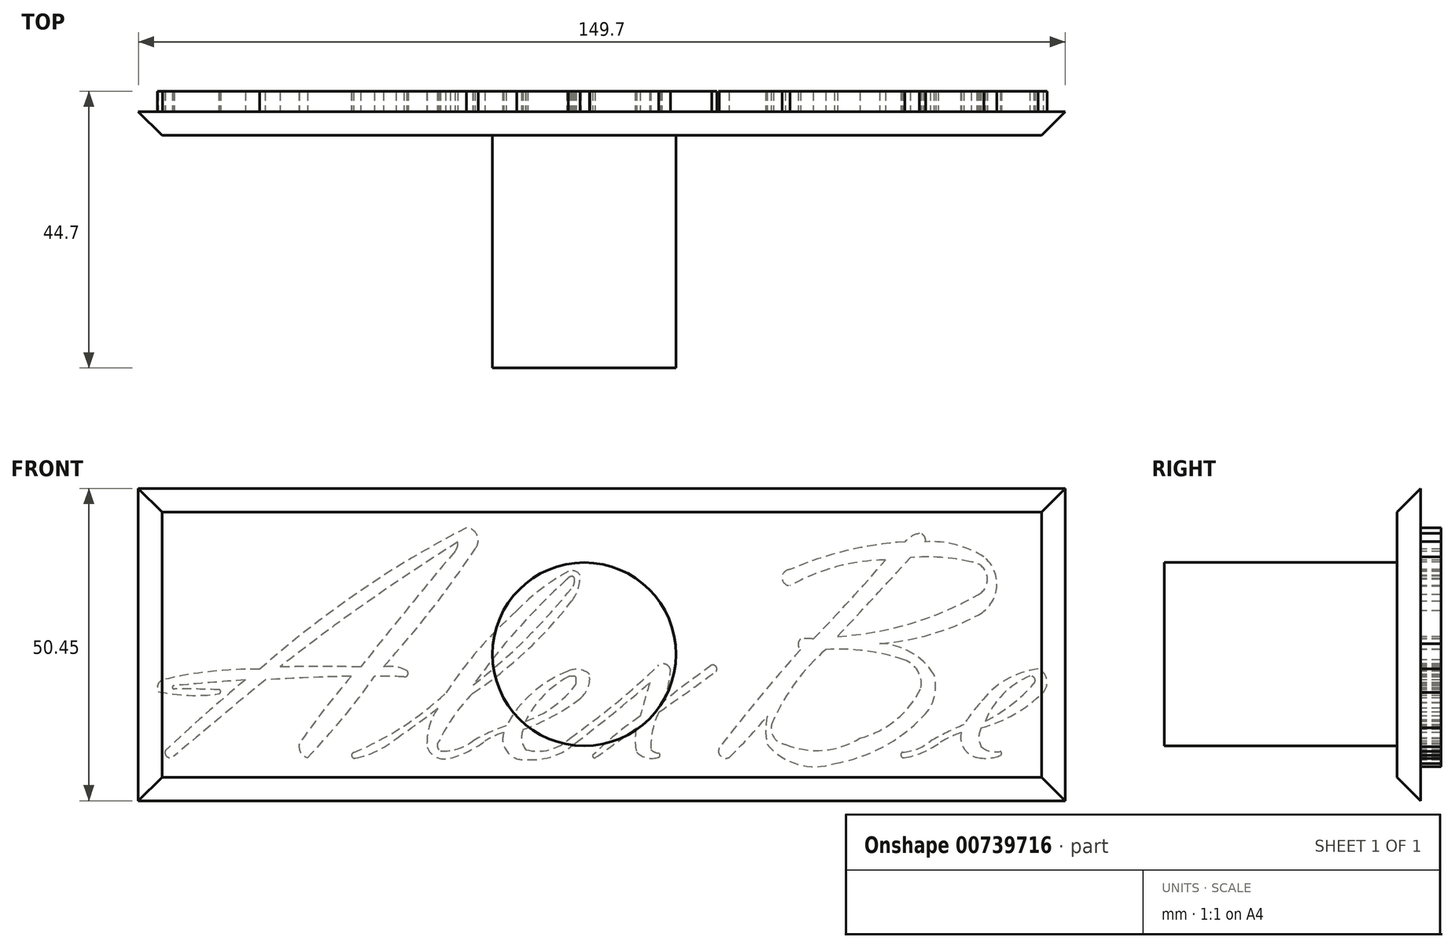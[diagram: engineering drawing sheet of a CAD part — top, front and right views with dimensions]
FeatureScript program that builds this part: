
annotation { "Feature Type Name" : "Feature", "Feature Type Description" : "" }
export const myFeature = defineFeature(function(context is Context, id is Id, definition is map)
    precondition{}
    {
        {
            var Q0;
            Q0=qCreatedBy(makeId("Front.planeOp"),FACE);
            var sketch = newSketch(context, id + "F0", { "sketchPlane" : qUnion([Q0])});
            skArc(sketch, "E0", {"start": v(-67.67, -1.55) * mm, "mid": v(-67.34, -2.53) * mm, "end": v(-66.3, -2.45) * mm});
            skArc(sketch, "E1", {"start": v(-54.74, 9.9) * mm, "mid": v(-61.3, 4.28) * mm, "end": v(-67.67, -1.55) * mm});
            skArc(sketch, "E2", {"start": v(-54.74, 9.9) * mm, "mid": v(-60.47, 9.47) * mm, "end": v(-66.2, 8.99) * mm});
            skArc(sketch, "E3", {"start": v(-66.2, 8.99) * mm, "mid": v(-66.51, 8.7) * mm, "end": v(-66.2, 8.43) * mm});
            skArc(sketch, "E4", {"start": v(-58.86, 8.3) * mm, "mid": v(-62.53, 8.42) * mm, "end": v(-66.2, 8.43) * mm});
            skArc(sketch, "E5", {"start": v(-59, 7.66) * mm, "mid": v(-58.74, 7.94) * mm, "end": v(-58.86, 8.3) * mm});
            skArc(sketch, "E6", {"start": v(-68.8, 8.02) * mm, "mid": v(-63.92, 7.4) * mm, "end": v(-59, 7.66) * mm});
            skArc(sketch, "E7", {"start": v(-68.12, 9.9) * mm, "mid": v(-68.87, 9.1) * mm, "end": v(-68.8, 8.02) * mm});
            skArc(sketch, "E8", {"start": v(-52.44, 11.62) * mm, "mid": v(-60.34, 11.27) * mm, "end": v(-68.12, 9.9) * mm});
            skArc(sketch, "E9", {"start": v(-19.01, 34.51) * mm, "mid": v(-36.44, 24.1) * mm, "end": v(-52.44, 11.62) * mm});
            skArc(sketch, "E10", {"start": v(-17.65, 31.1) * mm, "mid": v(-17.27, 33.22) * mm, "end": v(-19.01, 34.51) * mm});
            skArc(sketch, "E11", {"start": v(-32.44, 12.02) * mm, "mid": v(-24.67, 21.27) * mm, "end": v(-17.65, 31.1) * mm});
            skArc(sketch, "E12", {"start": v(-28.66, 11.42) * mm, "mid": v(-30.5, 12.02) * mm, "end": v(-32.44, 12.02) * mm});
            skArc(sketch, "E13", {"start": v(-29.11, 10.4) * mm, "mid": v(-28.5, 10.74) * mm, "end": v(-28.66, 11.42) * mm});
            skArc(sketch, "E14", {"start": v(-29.11, 10.4) * mm, "mid": v(-31.5, 10.5) * mm, "end": v(-33.87, 10.48) * mm});
            skArc(sketch, "E15", {"start": v(-44.7, -2.66) * mm, "mid": v(-39.03, 3.7) * mm, "end": v(-33.87, 10.48) * mm});
            skArc(sketch, "E16", {"start": v(-46.03, -0.44) * mm, "mid": v(-45.8, -1.81) * mm, "end": v(-44.7, -2.66) * mm});
            skArc(sketch, "E17", {"start": v(-37.62, 10.48) * mm, "mid": v(-41.98, 5.14) * mm, "end": v(-46.03, -0.44) * mm});
            skArc(sketch, "E18", {"start": v(-37.62, 10.48) * mm, "mid": v(-44.57, 10.29) * mm, "end": v(-51.51, 9.92) * mm});
            skArc(sketch, "E19", {"start": v(-51.51, 9.92) * mm, "mid": v(-58.92, 3.75) * mm, "end": v(-66.3, -2.45) * mm});
            skArc(sketch, "E20", {"start": v(-20.4, 32.19) * mm, "mid": v(-35.05, 22.49) * mm, "end": v(-49.15, 12.02) * mm});
            skArc(sketch, "E21", {"start": v(-20.88, 30.7) * mm, "mid": v(-20.49, 31.4) * mm, "end": v(-20.4, 32.19) * mm});
            skArc(sketch, "E22", {"start": v(-20.88, 30.7) * mm, "mid": v(-28.55, 21.4) * mm, "end": v(-36.1, 12.02) * mm});
            skArc(sketch, "E23", {"start": v(-36.1, 12.02) * mm, "mid": v(-42.62, 12.05) * mm, "end": v(-49.15, 12.02) * mm});
            skArc(sketch, "E24", {"start": v(-37.28, -1.84) * mm, "mid": v(-29.4, 2.28) * mm, "end": v(-22.4, 7.74) * mm});
            skArc(sketch, "E25", {"start": v(-10.88, 21.09) * mm, "mid": v(-17.07, 14.8) * mm, "end": v(-22.4, 7.74) * mm});
            skArc(sketch, "E26", {"start": v(-2.55, 27.44) * mm, "mid": v(-6.97, 24.6) * mm, "end": v(-10.88, 21.09) * mm});
            skArc(sketch, "E27", {"start": v(-0.68, 26.8) * mm, "mid": v(-1.48, 27.5) * mm, "end": v(-2.55, 27.44) * mm});
            skArc(sketch, "E28", {"start": v(-2.06, 22.6) * mm, "mid": v(-1, 24.57) * mm, "end": v(-0.68, 26.8) * mm});
            skArc(sketch, "E29", {"start": v(-18.01, 7.74) * mm, "mid": v(-9.43, 14.52) * mm, "end": v(-2.06, 22.6) * mm});
            skArc(sketch, "E30", {"start": v(-18.01, 7.74) * mm, "mid": v(-21.05, 4.1) * mm, "end": v(-23.44, 0) * mm});
            skArc(sketch, "E31", {"start": v(-23.44, 0) * mm, "mid": v(-23.73, -0.85) * mm, "end": v(-23.19, -1.57) * mm});
            skArc(sketch, "E32", {"start": v(-23.19, -1.57) * mm, "mid": v(-20.46, -1.24) * mm, "end": v(-18.01, 0) * mm});
            skArc(sketch, "E33", {"start": v(-12.6, 2.46) * mm, "mid": v(-15.38, 1.39) * mm, "end": v(-18.01, 0) * mm});
            skArc(sketch, "E34", {"start": v(-37.28, -1.84) * mm, "mid": v(-37.54, -2.43) * mm, "end": v(-36.99, -2.75) * mm});
            skArc(sketch, "E35", {"start": v(-36.99, -2.75) * mm, "mid": v(-33.5, -1.58) * mm, "end": v(-30.4, 0.4) * mm});
            skArc(sketch, "E36", {"start": v(-30.4, 0.4) * mm, "mid": v(-26.98, 2.81) * mm, "end": v(-23.65, 5.36) * mm});
            skArc(sketch, "E37", {"start": v(-23.65, 5.36) * mm, "mid": v(-25.04, 2.36) * mm, "end": v(-25.39, -0.92) * mm});
            skArc(sketch, "E38", {"start": v(-25.39, -0.92) * mm, "mid": v(-23.88, -2.57) * mm, "end": v(-21.65, -2.75) * mm});
            skArc(sketch, "E39", {"start": v(-21.65, -2.75) * mm, "mid": v(-18.72, -1.65) * mm, "end": v(-16.05, 0) * mm});
            skArc(sketch, "E40", {"start": v(-13.02, 1.38) * mm, "mid": v(-14.6, 0.81) * mm, "end": v(-16.05, 0) * mm});
            skArc(sketch, "E41", {"start": v(-2.8, 26.14) * mm, "mid": v(-10.84, 18.02) * mm, "end": v(-17.94, 9.06) * mm});
            skArc(sketch, "E42", {"start": v(-1.95, 26.65) * mm, "mid": v(-2.44, 26.5) * mm, "end": v(-2.8, 26.14) * mm});
            skArc(sketch, "E43", {"start": v(-1.78, 25.05) * mm, "mid": v(-1.58, 25.65) * mm, "end": v(-1.57, 26.28) * mm});
            skArc(sketch, "E44", {"start": v(-1.57, 26.28) * mm, "mid": v(-1.7, 26.53) * mm, "end": v(-1.95, 26.65) * mm});
            skArc(sketch, "E45", {"start": v(-17.94, 9.06) * mm, "mid": v(-9.4, 16.59) * mm, "end": v(-1.78, 25.05) * mm});
            skArc(sketch, "E46", {"start": v(-2.63, 11.32) * mm, "mid": v(-8.41, 7.78) * mm, "end": v(-12.6, 2.46) * mm});
            skArc(sketch, "E47", {"start": v(0.83, 10.82) * mm, "mid": v(-0.83, 11.58) * mm, "end": v(-2.63, 11.32) * mm});
            skArc(sketch, "E48", {"start": v(-0.57, 6.97) * mm, "mid": v(0.64, 8.7) * mm, "end": v(0.83, 10.82) * mm});
            skArc(sketch, "E49", {"start": v(-9.88, 1.9) * mm, "mid": v(-5.02, 4.05) * mm, "end": v(-0.57, 6.97) * mm});
            skArc(sketch, "E50", {"start": v(-9.88, 1.9) * mm, "mid": v(-10.09, 0.2) * mm, "end": v(-9.43, -1.36) * mm});
            skArc(sketch, "E51", {"start": v(-9.43, -1.36) * mm, "mid": v(-5.63, -1.38) * mm, "end": v(-2.32, 0.47) * mm});
            skArc(sketch, "E52", {"start": v(-2.32, 0.47) * mm, "mid": v(5.08, 6.13) * mm, "end": v(12.06, 12.3) * mm});
            skArc(sketch, "E53", {"start": v(13.91, 11.64) * mm, "mid": v(13.15, 12.43) * mm, "end": v(12.06, 12.3) * mm});
            skArc(sketch, "E54", {"start": v(12.55, 6.23) * mm, "mid": v(13.55, 8.85) * mm, "end": v(13.91, 11.64) * mm});
            skArc(sketch, "E55", {"start": v(20.63, 12.3) * mm, "mid": v(16.55, 9.32) * mm, "end": v(12.55, 6.23) * mm});
            skArc(sketch, "E56", {"start": v(21.32, 11.3) * mm, "mid": v(21.3, 12.03) * mm, "end": v(20.63, 12.3) * mm});
            skArc(sketch, "E57", {"start": v(12.06, 4.7) * mm, "mid": v(16.7, 7.97) * mm, "end": v(21.32, 11.3) * mm});
            skArc(sketch, "E58", {"start": v(12.06, 4.7) * mm, "mid": v(11.04, 1.74) * mm, "end": v(10.74, -1.36) * mm});
            skArc(sketch, "E59", {"start": v(10.74, -1.36) * mm, "mid": v(11.35, -1.75) * mm, "end": v(12.06, -1.94) * mm});
            skArc(sketch, "E60", {"start": v(12.06, -2.59) * mm, "mid": v(12.25, -2.26) * mm, "end": v(12.06, -1.94) * mm});
            skArc(sketch, "E61", {"start": v(8.45, -1.77) * mm, "mid": v(10.14, -2.69) * mm, "end": v(12.06, -2.59) * mm});
            skArc(sketch, "E62", {"start": v(8.45, 2.16) * mm, "mid": v(8.22, 0.2) * mm, "end": v(8.45, -1.77) * mm});
            skArc(sketch, "E63", {"start": v(1.77, -2.69) * mm, "mid": v(5.12, -0.27) * mm, "end": v(8.45, 2.16) * mm});
            skArc(sketch, "E64", {"start": v(1.34, -2.3) * mm, "mid": v(1.46, -2.6) * mm, "end": v(1.77, -2.69) * mm});
            skArc(sketch, "E65", {"start": v(9.03, 4.04) * mm, "mid": v(5.05, 1.04) * mm, "end": v(1.34, -2.3) * mm});
            skArc(sketch, "E66", {"start": v(10.6, 9.48) * mm, "mid": v(9.8, 6.77) * mm, "end": v(9.03, 4.04) * mm});
            skArc(sketch, "E67", {"start": v(-1.45, -0.3) * mm, "mid": v(4.66, 4.48) * mm, "end": v(10.6, 9.48) * mm});
            skArc(sketch, "E68", {"start": v(-9.15, -2.96) * mm, "mid": v(-5.02, -2.42) * mm, "end": v(-1.45, -0.3) * mm});
            skArc(sketch, "E69", {"start": v(-13.02, 1.38) * mm, "mid": v(-12.3, -1.87) * mm, "end": v(-9.15, -2.96) * mm});
            skArc(sketch, "E70", {"start": v(-2.58, 10.44) * mm, "mid": v(-6.58, 7.34) * mm, "end": v(-9.51, 3.21) * mm});
            skArc(sketch, "E71", {"start": v(-1.35, 10.44) * mm, "mid": v(-1.96, 10.47) * mm, "end": v(-2.58, 10.44) * mm});
            skArc(sketch, "E72", {"start": v(-1.35, 9.16) * mm, "mid": v(-1.31, 9.8) * mm, "end": v(-1.35, 10.44) * mm});
            skArc(sketch, "E73", {"start": v(-9.51, 3.21) * mm, "mid": v(-4.99, 5.58) * mm, "end": v(-1.35, 9.16) * mm});
            skArc(sketch, "E74", {"start": v(34.94, 14.8) * mm, "mid": v(28.22, 6.97) * mm, "end": v(21.8, -1.1) * mm});
            skArc(sketch, "E75", {"start": v(34.94, 16.52) * mm, "mid": v(34.57, 15.66) * mm, "end": v(34.94, 14.8) * mm});
            skArc(sketch, "E76", {"start": v(37, 16.52) * mm, "mid": v(35.97, 16.6) * mm, "end": v(34.94, 16.52) * mm});
            skArc(sketch, "E77", {"start": v(37, 16.52) * mm, "mid": v(42.95, 22.82) * mm, "end": v(48.69, 29.31) * mm});
            skArc(sketch, "E78", {"start": v(48.69, 29.31) * mm, "mid": v(40.7, 28.18) * mm, "end": v(33.22, 25.13) * mm});
            skArc(sketch, "E79", {"start": v(33.22, 27.73) * mm, "mid": v(31.96, 26.43) * mm, "end": v(33.22, 25.13) * mm});
            skArc(sketch, "E80", {"start": v(51.76, 32.23) * mm, "mid": v(42.3, 30.77) * mm, "end": v(33.22, 27.73) * mm});
            skArc(sketch, "E81", {"start": v(54.13, 33.57) * mm, "mid": v(52.83, 33.1) * mm, "end": v(51.76, 32.23) * mm});
            skArc(sketch, "E82", {"start": v(55.08, 32.23) * mm, "mid": v(54.93, 33.13) * mm, "end": v(54.13, 33.57) * mm});
            skArc(sketch, "E83", {"start": v(64.56, 29.79) * mm, "mid": v(60.01, 31.75) * mm, "end": v(55.08, 32.23) * mm});
            skArc(sketch, "E84", {"start": v(63.67, 20.41) * mm, "mid": v(66.64, 24.86) * mm, "end": v(64.56, 29.79) * mm});
            skArc(sketch, "E85", {"start": v(47.72, 15.78) * mm, "mid": v(55.94, 17.26) * mm, "end": v(63.67, 20.41) * mm});
            skArc(sketch, "E86", {"start": v(56.48, 10.78) * mm, "mid": v(52.73, 14.38) * mm, "end": v(47.72, 15.78) * mm});
            skArc(sketch, "E87", {"start": v(54.77, 4.04) * mm, "mid": v(56.56, 7.17) * mm, "end": v(56.48, 10.78) * mm});
            skArc(sketch, "E88", {"start": v(40.43, -3.59) * mm, "mid": v(48.22, -0.94) * mm, "end": v(54.77, 4.04) * mm});
            skArc(sketch, "E89", {"start": v(29.55, -0.51) * mm, "mid": v(34.51, -3.74) * mm, "end": v(40.43, -3.59) * mm});
            skArc(sketch, "E90", {"start": v(29.55, 4.04) * mm, "mid": v(29.31, 1.77) * mm, "end": v(29.55, -0.51) * mm});
            skArc(sketch, "E91", {"start": v(23.38, -2.65) * mm, "mid": v(26.57, 0.6) * mm, "end": v(29.55, 4.04) * mm});
            skArc(sketch, "E92", {"start": v(21.8, -1.1) * mm, "mid": v(22.05, -2.43) * mm, "end": v(23.38, -2.65) * mm});
            skArc(sketch, "E93", {"start": v(39.02, 14.83) * mm, "mid": v(34.2, 9.59) * mm, "end": v(30.6, 3.45) * mm});
            skArc(sketch, "E94", {"start": v(30.6, 3.45) * mm, "mid": v(30.45, 0.95) * mm, "end": v(32.49, -0.51) * mm});
            skArc(sketch, "E95", {"start": v(32.49, -0.51) * mm, "mid": v(38.63, -1.46) * mm, "end": v(44.54, 0.5) * mm});
            skArc(sketch, "E96", {"start": v(44.54, 0.5) * mm, "mid": v(50.38, 3.47) * mm, "end": v(54.41, 8.64) * mm});
            skArc(sketch, "E97", {"start": v(54.41, 8.64) * mm, "mid": v(53.86, 11.4) * mm, "end": v(51.68, 13.16) * mm});
            skArc(sketch, "E98", {"start": v(51.68, 13.16) * mm, "mid": v(45.43, 14.6) * mm, "end": v(39.02, 14.83) * mm});
            skArc(sketch, "E99", {"start": v(62.49, 28.98) * mm, "mid": v(57.6, 29.7) * mm, "end": v(52.67, 29.65) * mm});
            skArc(sketch, "E100", {"start": v(63.66, 23.68) * mm, "mid": v(65.07, 26.77) * mm, "end": v(62.49, 28.98) * mm});
            skArc(sketch, "E101", {"start": v(40.9, 16.93) * mm, "mid": v(52.66, 19) * mm, "end": v(63.66, 23.68) * mm});
            skArc(sketch, "E102", {"start": v(40.9, 16.93) * mm, "mid": v(46.8, 23.26) * mm, "end": v(52.67, 29.65) * mm});
            skArc(sketch, "E103", {"start": v(64.13, -0.9) * mm, "mid": v(65.58, -1.63) * mm, "end": v(67.2, -1.65) * mm});
            skArc(sketch, "E104", {"start": v(64.13, 2.18) * mm, "mid": v(63.73, 0.64) * mm, "end": v(64.13, -0.9) * mm});
            skArc(sketch, "E105", {"start": v(64.13, 2.18) * mm, "mid": v(69.51, 4.38) * mm, "end": v(74.15, 7.9) * mm});
            skArc(sketch, "E106", {"start": v(74.15, 7.9) * mm, "mid": v(74.7, 10) * mm, "end": v(73.33, 11.7) * mm});
            skArc(sketch, "E107", {"start": v(63.96, 6.17) * mm, "mid": v(62.55, 4.5) * mm, "end": v(61.34, 2.66) * mm});
            skArc(sketch, "E108", {"start": v(61.34, 2.66) * mm, "mid": v(58.58, 1.43) * mm, "end": v(55.93, 0) * mm});
            skArc(sketch, "E109", {"start": v(51.4, -1.78) * mm, "mid": v(53.8, -1.24) * mm, "end": v(55.93, 0) * mm});
            skArc(sketch, "E110", {"start": v(51.4, -1.78) * mm, "mid": v(51.15, -2.35) * mm, "end": v(51.68, -2.67) * mm});
            skArc(sketch, "E111", {"start": v(51.68, -2.67) * mm, "mid": v(54.55, -1.86) * mm, "end": v(57.15, -0.42) * mm});
            skArc(sketch, "E112", {"start": v(60.92, 1.43) * mm, "mid": v(58.99, 0.6) * mm, "end": v(57.15, -0.42) * mm});
            skArc(sketch, "E113", {"start": v(60.92, 1.43) * mm, "mid": v(61.3, -1.12) * mm, "end": v(63.4, -2.62) * mm});
            skArc(sketch, "E114", {"start": v(63.4, -2.62) * mm, "mid": v(65.36, -2.73) * mm, "end": v(67.28, -2.28) * mm});
            skArc(sketch, "E115", {"start": v(67.28, -2.28) * mm, "mid": v(67.42, -1.95) * mm, "end": v(67.2, -1.65) * mm});
            skArc(sketch, "E116", {"start": v(72, 10.54) * mm, "mid": v(67.65, 7.62) * mm, "end": v(64.78, 3.24) * mm});
            skArc(sketch, "E117", {"start": v(72.64, 9.32) * mm, "mid": v(72.76, 10.15) * mm, "end": v(72, 10.54) * mm});
            skArc(sketch, "E118", {"start": v(64.78, 3.24) * mm, "mid": v(69, 5.9) * mm, "end": v(72.64, 9.32) * mm});
            skArc(sketch, "E119", {"start": v(73.33, 11.7) * mm, "mid": v(68.08, 9.9) * mm, "end": v(63.96, 6.17) * mm});
            skSolve(sketch);
        }
        {
            var Q0;
            Q0=qCreatedBy(makeId("Front.planeOp"),FACE);
            var sketch = newSketch(context, id + "F1", { "sketchPlane" : qUnion([Q0])});
            skLineSegment(sketch, "E120.bottom", {"start": v(-73.28, 42.1) * mm, "end": v(78.96, 42.1) * mm});
            skLineSegment(sketch, "E120.top", {"start": v(-73.28, -10.9) * mm, "end": v(78.96, -10.9) * mm});
            skLineSegment(sketch, "E120.left", {"start": v(-73.28, 42.1) * mm, "end": v(-73.28, -10.9) * mm});
            skLineSegment(sketch, "E120.right", {"start": v(78.96, 42.1) * mm, "end": v(78.96, -10.9) * mm});
            skSolve(sketch);
        }
        {
            var Q0;
            Q0 = qSketchRegion(id + "F1", true);
            var Q1;
            Q1=makeQuery(id+"F1.imprint","IMPRINT",FACE,{"disambiguationData":[TD([[makeQuery(id+"F1.imprint","IMPRINT",EDGE,{"derivedFrom":sQuery(id+"F1.wireOp",EDGE,"E120.bottom")}),-1.0]])]});
            extrude(context, id + "F2", {"entities" : qUnion([Q0, Q1]), "oppositeDirection" : true, "depth" : 3.8 * mm, "offsetDistance" : 25.4 * mm});
        }
        {
            var Q0;
            Q0 = qSketchRegion(id + "F0", true);
            extrude(context, id + "F3", {"entities" : qUnion([Q0]), "operationType" : NewBodyOperationType.ADD, "oppositeDirection" : true, "depth" : 7.11 * mm, "offsetDistance" : 25.4 * mm});
        }
        {
            var Q0;
            Q0=qCreatedBy(makeId("Front.planeOp"),FACE);
            var sketch = newSketch(context, id + "F4", { "sketchPlane" : qUnion([Q0])});
            skCircle(sketch, "E121", {"center": v(0, 14.06) * mm, "radius": 14.82 * mm});
            skSolve(sketch);
        }
        {
            var Q0;
            Q0 = qSketchRegion(id + "F4", true);
            extrude(context, id + "F5", {"entities" : qUnion([Q0]), "operationType" : NewBodyOperationType.ADD, "depth" : 37.6 * mm, "offsetDistance" : 25.4 * mm});
        }
        {
            var Q0;
            Q0=makeQuery(id+"F2.opExtrude","CAP_EDGE",EDGE,{"disambiguationData":[OSD([sQuery(id+"F1.wireOp",EDGE,"E120.bottom")])],"isStart":true});
            var Q1;
            Q1=makeQuery(id+"F2.opExtrude","CAP_EDGE",EDGE,{"disambiguationData":[OSD([sQuery(id+"F1.wireOp",EDGE,"E120.left")])],"isStart":true});
            var Q2;
            Q2=makeQuery(id+"F2.opExtrude","CAP_EDGE",EDGE,{"disambiguationData":[OSD([sQuery(id+"F1.wireOp",EDGE,"E120.top")])],"isStart":true});
            var Q3;
            Q3=makeQuery(id+"F2.opExtrude","CAP_EDGE",EDGE,{"disambiguationData":[OSD([sQuery(id+"F1.wireOp",EDGE,"E120.right")])],"isStart":true});
            chamfer(context, id + "F6", {"entities" : qUnion([Q0, Q1, Q2, Q3]), "width" : 5.08 * mm, "tangentPropagation" : true});
        }
    });
